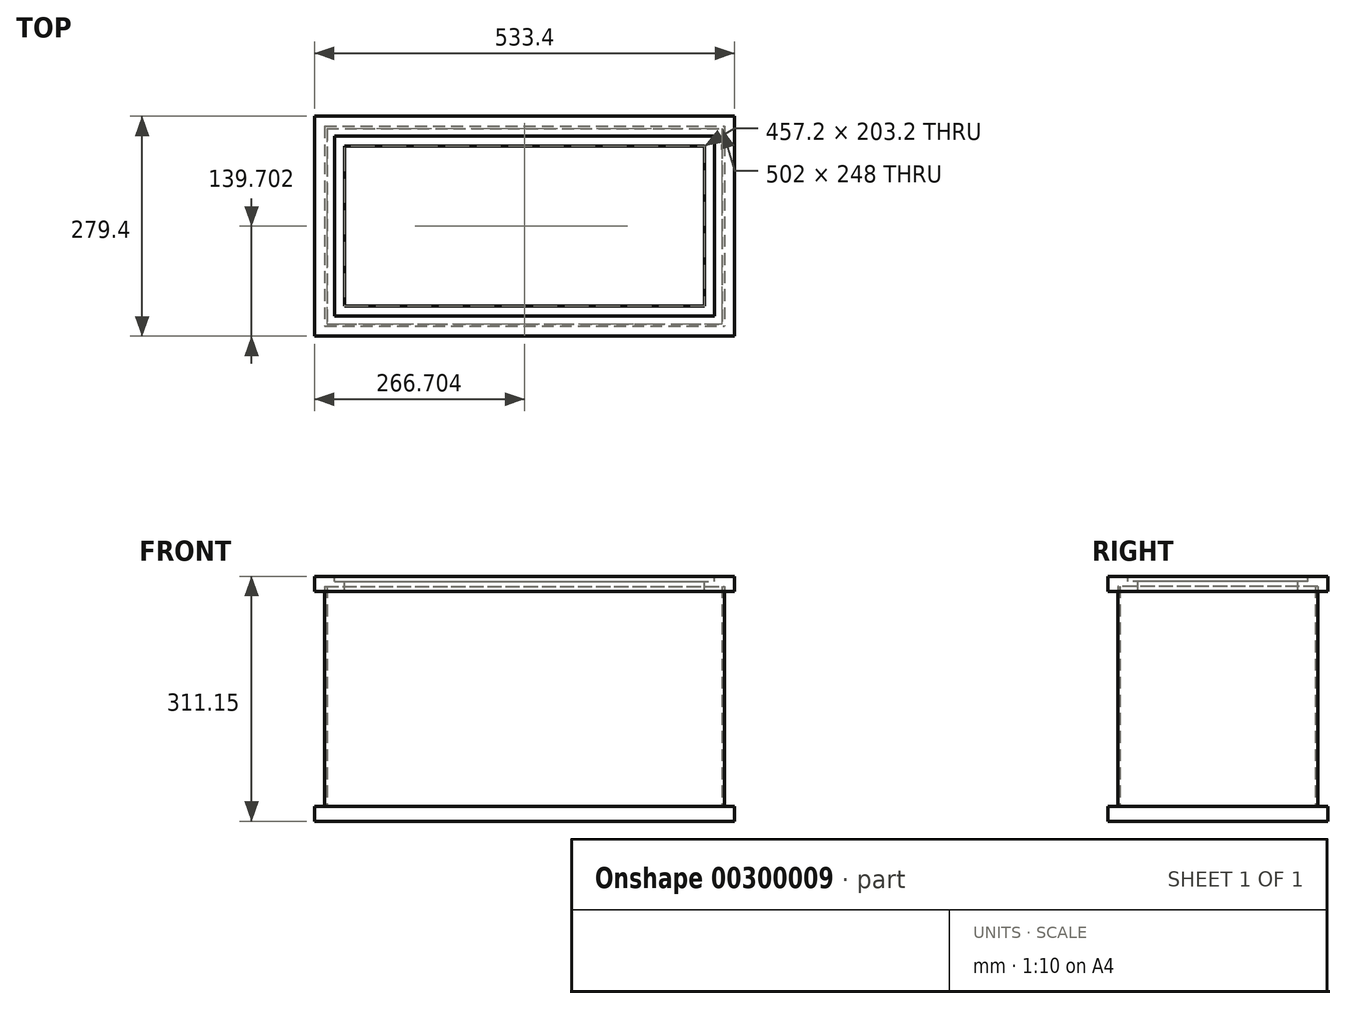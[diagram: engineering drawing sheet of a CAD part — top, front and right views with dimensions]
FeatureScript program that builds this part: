
annotation { "Feature Type Name" : "Feature", "Feature Type Description" : "" }
export const myFeature = defineFeature(function(context is Context, id is Id, definition is map)
    precondition{}
    {
        {
            var Q0;
            Q0=qCreatedBy(makeId("Top.planeOp"),FACE);
            var sketch = newSketch(context, id + "F0", { "sketchPlane" : qUnion([Q0])});
            skLineSegment(sketch, "E0.bottom", {"start": v(-249.28, 176.41) * mm, "end": v(284.12, 176.41) * mm});
            skLineSegment(sketch, "E0.top", {"start": v(-249.28, -102.99) * mm, "end": v(284.12, -102.99) * mm});
            skLineSegment(sketch, "E0.left", {"start": v(-249.28, 176.41) * mm, "end": v(-249.28, -102.99) * mm});
            skLineSegment(sketch, "E0.right", {"start": v(284.12, 176.41) * mm, "end": v(284.12, -102.99) * mm});
            skSolve(sketch);
        }
        {
            var Q0;
            Q0 = qSketchRegion(id + "F0", true);
            extrude(context, id + "F1", {"entities" : qUnion([Q0]), "depth" : 19.05 * mm});
        }
        {
            var Q0;
            Q0=makeQuery(id+"F1.opExtrude","CAP_FACE",FACE,{"disambiguationData":[OSD([sQuery(id+"F0.wireOp",EDGE,"E0.bottom"),sQuery(id+"F0.wireOp",EDGE,"E0.top"),sQuery(id+"F0.wireOp",EDGE,"E0.left"),sQuery(id+"F0.wireOp",EDGE,"E0.right")])],"isStart":false});
            var sketch = newSketch(context, id + "F2", { "sketchPlane" : qUnion([Q0])});
            skLineSegment(sketch, "E1.bottom", {"start": v(-236.58, 163.71) * mm, "end": v(271.42, 163.71) * mm});
            skLineSegment(sketch, "E1.top", {"start": v(-236.58, -90.29) * mm, "end": v(271.42, -90.29) * mm});
            skLineSegment(sketch, "E1.left", {"start": v(-236.58, 163.71) * mm, "end": v(-236.58, -90.29) * mm});
            skLineSegment(sketch, "E1.right", {"start": v(271.42, 163.71) * mm, "end": v(271.42, -90.29) * mm});
            skLineSegment(sketch, "E2.0", {"start": v(-233.58, 160.71) * mm, "end": v(268.42, 160.71) * mm});
            skLineSegment(sketch, "E2.1", {"start": v(-233.58, 160.71) * mm, "end": v(-233.58, -87.29) * mm});
            skLineSegment(sketch, "E2.2", {"start": v(-233.58, -87.29) * mm, "end": v(268.42, -87.29) * mm});
            skLineSegment(sketch, "E2.3", {"start": v(268.42, 160.71) * mm, "end": v(268.42, -87.29) * mm});
            skSolve(sketch);
        }
        {
            var Q0;
            Q0 = qSketchRegion(id + "F2", true);
            extrude(context, id + "F3", {"entities" : qUnion([Q0]), "depth" : 279.4 * mm});
        }
        {
            var Q0;
            Q0=makeQuery(id+"F3.opExtrude","CAP_FACE",FACE,{"disambiguationData":[OSD([sQuery(id+"F2.wireOp",EDGE,"E1.bottom"),sQuery(id+"F2.wireOp",EDGE,"E1.top"),sQuery(id+"F2.wireOp",EDGE,"E1.left"),sQuery(id+"F2.wireOp",EDGE,"E1.right"),sQuery(id+"F2.wireOp",EDGE,"E2.0"),sQuery(id+"F2.wireOp",EDGE,"E2.1"),sQuery(id+"F2.wireOp",EDGE,"E2.2"),sQuery(id+"F2.wireOp",EDGE,"E2.3")])],"isStart":false});
            var sketch = newSketch(context, id + "F4", { "sketchPlane" : qUnion([Q0])});
            skLineSegment(sketch, "E3.bottom", {"start": v(-249.28, 176.41) * mm, "end": v(284.12, 176.41) * mm});
            skLineSegment(sketch, "E3.top", {"start": v(-249.28, -102.99) * mm, "end": v(284.12, -102.99) * mm});
            skLineSegment(sketch, "E3.left", {"start": v(-249.28, 176.41) * mm, "end": v(-249.28, -102.99) * mm});
            skLineSegment(sketch, "E3.right", {"start": v(284.12, 176.41) * mm, "end": v(284.12, -102.99) * mm});
            skSolve(sketch);
        }
        {
            var Q0;
            Q0 = qSketchRegion(id + "F4", true);
            extrude(context, id + "F5", {"entities" : qUnion([Q0]), "endBound" : BoundingType.SYMMETRIC, "oppositeDirection" : true, "depth" : 12.7 * mm});
        }
        {
            var Q0;
            Q0=makeQuery(id+"F5.opExtrude","CAP_FACE",FACE,{"disambiguationData":[OSD([sQuery(id+"F4.wireOp",EDGE,"E3.bottom"),sQuery(id+"F4.wireOp",EDGE,"E3.top"),sQuery(id+"F4.wireOp",EDGE,"E3.left"),sQuery(id+"F4.wireOp",EDGE,"E3.right")])],"isStart":true});
            var sketch = newSketch(context, id + "F6", { "sketchPlane" : qUnion([Q0])});
            skLineSegment(sketch, "E4.bottom", {"start": v(-249.28, 176.41) * mm, "end": v(284.12, 176.41) * mm});
            skLineSegment(sketch, "E4.top", {"start": v(-249.28, -102.99) * mm, "end": v(284.12, -102.99) * mm});
            skLineSegment(sketch, "E4.left", {"start": v(-249.28, 176.41) * mm, "end": v(-249.28, -102.99) * mm});
            skLineSegment(sketch, "E4.right", {"start": v(284.12, 176.41) * mm, "end": v(284.12, -102.99) * mm});
            skSolve(sketch);
        }
        {
            var Q0;
            Q0 = qSketchRegion(id + "F6", true);
            extrude(context, id + "F7", {"entities" : qUnion([Q0]), "operationType" : NewBodyOperationType.ADD, "depth" : 6.35 * mm});
        }
        {
            var Q0;
            Q0=makeQuery(id+"F7.opExtrude","CAP_FACE",FACE,{"disambiguationData":[OSD([sQuery(id+"F6.wireOp",EDGE,"E4.bottom"),sQuery(id+"F6.wireOp",EDGE,"E4.top"),sQuery(id+"F6.wireOp",EDGE,"E4.left"),sQuery(id+"F6.wireOp",EDGE,"E4.right")])],"isStart":false});
            var sketch = newSketch(context, id + "F8", { "sketchPlane" : qUnion([Q0])});
            skLineSegment(sketch, "E5.bottom", {"start": v(-223.88, 151.01) * mm, "end": v(258.72, 151.01) * mm});
            skLineSegment(sketch, "E5.top", {"start": v(-223.88, -77.59) * mm, "end": v(258.72, -77.59) * mm});
            skLineSegment(sketch, "E5.left", {"start": v(-223.88, 151.01) * mm, "end": v(-223.88, -77.59) * mm});
            skLineSegment(sketch, "E5.right", {"start": v(258.72, 151.01) * mm, "end": v(258.72, -77.59) * mm});
            skSolve(sketch);
        }
        {
            var Q0;
            Q0 = qSketchRegion(id + "F8", true);
            extrude(context, id + "F9", {"entities" : qUnion([Q0]), "operationType" : NewBodyOperationType.REMOVE, "oppositeDirection" : true, "depth" : 6.35 * mm});
        }
        {
            var Q0;
            Q0=makeQuery(id+"F9.boolean.opBoolean","COPY",FACE,{"derivedFrom":makeQuery(id+"F9.opExtrude","CAP_FACE",FACE,{"disambiguationData":[OSD([sQuery(id+"F8.wireOp",EDGE,"E5.bottom"),sQuery(id+"F8.wireOp",EDGE,"E5.top"),sQuery(id+"F8.wireOp",EDGE,"E5.left"),sQuery(id+"F8.wireOp",EDGE,"E5.right")])],"isStart":false})});
            var sketch = newSketch(context, id + "F10", { "sketchPlane" : qUnion([Q0])});
            skLineSegment(sketch, "E6.bottom", {"start": v(-211.18, 138.31) * mm, "end": v(246.02, 138.31) * mm});
            skLineSegment(sketch, "E6.top", {"start": v(-211.18, -64.89) * mm, "end": v(246.02, -64.89) * mm});
            skLineSegment(sketch, "E6.left", {"start": v(-211.18, 138.31) * mm, "end": v(-211.18, -64.89) * mm});
            skLineSegment(sketch, "E6.right", {"start": v(246.02, 138.31) * mm, "end": v(246.02, -64.89) * mm});
            skSolve(sketch);
        }
        {
            var Q0;
            Q0 = qSketchRegion(id + "F10", true);
            extrude(context, id + "F11", {"entities" : qUnion([Q0]), "operationType" : NewBodyOperationType.REMOVE, "oppositeDirection" : true, "depth" : 25.4 * mm});
        }
    });
